# Revit family: Practibox_S_cofrecito_saliente_18_módulos_réf_137106_a_137219
name_source: partatom
category: Equipement électrique
revit_build: Autodesk Revit 2018 (Build: 20170223_1515(x64)
units: mm (PartAtom-declared; Revit-internal decimal feet)

## family parameters
Basée sur le plan de construction = Non
Configuration du panneau = Deux colonnes, circuits au sein
Cote de connecteur circulaire = Utiliser le diamètre
Couper avec des vides une fois chargée = Non
Numéro OmniClass = 23.80.30.11.17
Partagée = Non
Point de calcul de pièce = Non
Titre OmniClass = Distribution Boards and Control Panels
Toujours verticalement = Oui
Type d'élément = Tableau de raccordement

## types (16) — shared parameters
Condiciones Generales de Uso = https://export.legrand.com
Fabricant = "Legrand"
URL = www.legrand.com
anchura = 436 mm  [stored 1.43045 ft]
profundidad = 320 mm  [stored 1.04987 ft]

## per-type parameters (varying)
| type | 1R | 2R | 3R | 4R | Altura | Bornas N | Bornas T | Ina | puerta B 1 r | puerta B 2 r | puerta B 3 r | puerta B 4 r | puerta T 1 r | puerta T 2 r | puerta T 3 r | puerta T 4 r | puerta blanca | puerta transparencia | tamaño |
| Practibox_S_cofrecito_saliente_18_módulos_137106 | Oui | Non | Non | Non | 236 mm |  |  | 63A | Oui | Non | Non | Non | Non | Non | Non | Non | Oui | Non | 1 fila |
| Practibox_S_cofrecito_saliente_36_módulos_137107 | Non | Oui | Non | Non | 386 mm  [stored 1.2664 ft] |  |  | 90A | Non | Oui | Non | Non | Non | Non | Non | Non | Oui | Non | 2 fila |
| Practibox_S_cofrecito_saliente_54_módulos_137108 | Non | Non | Oui | Non | 616 mm  [stored 2.021 ft] |  |  | 90A | Non | Non | Oui | Non | Non | Non | Non | Non | Oui | Non | 3 fila |
| Practibox_S_cofrecito_saliente_72_módulos_137109 | Non | Non | Non | Oui | 766 mm  [stored 2.51312 ft] |  |  | 90A | Non | Non | Non | Oui | Non | Non | Non | Non | Oui | Non | 4 fila |
| Practibox_S_cofrecito_saliente_18_módulos_137116 | Oui | Non | Non | Non | 236 mm |  |  | 63A | Non | Non | Non | Non | Oui | Non | Non | Non | Non | Oui | 1 fila |
| Practibox_S_cofrecito_saliente_18_módulos_137216 | Oui | Non | Non | Non | 236 mm | 27 salidas Icc 10kA | 27 salidas Icc 10kA | 63A | Non | Non | Non | Non | Oui | Non | Non | Non | Non | Oui | 1 fila |
| Practibox_S_cofrecito_saliente_18_módulos_137206 | Oui | Non | Non | Non | 236 mm | 27 salidas Icc 10kA | 27 salidas Icc 10kA | 63A | Oui | Non | Non | Non | Non | Non | Non | Non | Oui | Non | 1 fila |
| Practibox_S_cofrecito_saliente_36_módulos_137117 | Non | Oui | Non | Non | 386 mm  [stored 1.2664 ft] |  |  | 90A | Non | Non | Non | Non | Non | Oui | Non | Non | Non | Oui | 2 fila |
| Practibox_S_cofrecito_saliente_36_módulos_137207 | Non | Oui | Non | Non | 386 mm  [stored 1.2664 ft] | 27 salidas Icc 10kA | 27 salidas Icc 10kA | 90A | Non | Oui | Non | Non | Non | Non | Non | Non | Oui | Non | 2 fila |
| Practibox_S_cofrecito_saliente_36_módulos_137217 | Non | Oui | Non | Non | 386 mm  [stored 1.2664 ft] | 27 salidas Icc 10kA | 27 salidas Icc 10kA | 90A | Non | Oui | Non | Non | Non | Non | Non | Non | Oui | Non | 2 fila |
| Practibox_S_cofrecito_saliente_54_módulos_137118 | Non | Non | Oui | Non | 616 mm  [stored 2.021 ft] |  |  | 90A | Non | Non | Non | Non | Non | Non | Oui | Non | Non | Oui | 3 fila |
| Practibox_S_cofrecito_saliente_54_módulos_137218 | Non | Non | Oui | Non | 616 mm  [stored 2.021 ft] | 27 salidas Icc 10kA | 27 salidas Icc 10kA | 90A | Non | Non | Non | Non | Non | Non | Oui | Non | Non | Oui | 3 fila |
| Practibox_S_cofrecito_saliente_54_módulos_137208 | Non | Non | Oui | Non | 616 mm  [stored 2.021 ft] | 27 salidas Icc 10kA | 27 salidas Icc 10kA | 90A | Non | Non | Oui | Non | Non | Non | Non | Non | Oui | Non | 3 fila |
| Practibox_S_cofrecito_saliente_72_módulos_137119 | Non | Non | Non | Oui | 766 mm  [stored 2.51312 ft] |  |  | 90A | Non | Non | Non | Non | Non | Non | Non | Oui | Non | Oui | 4 fila |
| Practibox_S_cofrecito_saliente_72_módulos_137209 | Non | Non | Non | Oui | 766 mm  [stored 2.51312 ft] | 27 salidas Icc 10kA | 27 salidas Icc 10kA | 90A | Non | Non | Non | Oui | Non | Non | Non | Non | Oui | Non | 4 fila |
| Practibox_S_cofrecito_saliente_72_módulos_137219 | Non | Non | Non | Oui | 766 mm  [stored 2.51312 ft] | 27 salidas Icc 10kA | 27 salidas Icc 10kA | 90A | Non | Non | Non | Non | Non | Non | Non | Oui | Non | Oui | 4 fila |

note: column(s) folded — value = type name in every type: Description

note: [stored X ft] marks values corroborated as IEEE doubles in the binary element streams (Revit-internal decimal feet)
